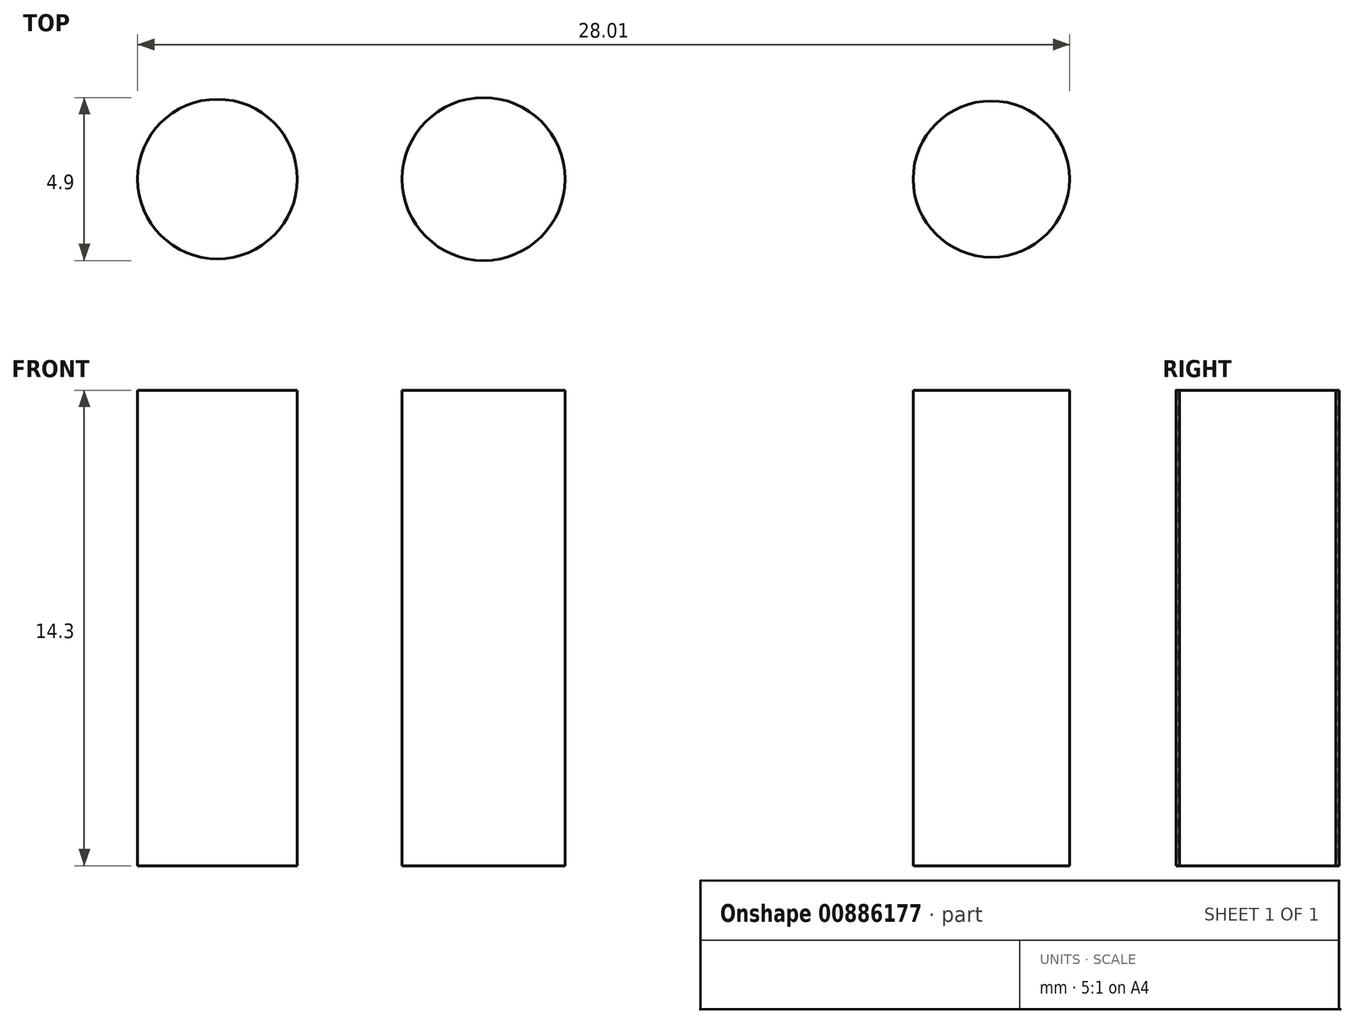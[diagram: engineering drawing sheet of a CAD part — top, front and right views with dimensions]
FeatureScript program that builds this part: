
annotation { "Feature Type Name" : "Feature", "Feature Type Description" : "" }
export const myFeature = defineFeature(function(context is Context, id is Id, definition is map)
    precondition{}
    {
        {
            var Q0;
            Q0=qCreatedBy(makeId("Top.planeOp"), FACE);
            var sketch = newSketch(context, id + "F0", { "sketchPlane" : qUnion([Q0])});
            skCircle(sketch, "E0", {"center": v(0, 0) * mm, "radius": 2.45 * mm});
            skCircle(sketch, "E1", {"center": v(-8, 0) * mm, "radius": 2.4 * mm});
            skCircle(sketch, "E2", {"center": v(15.26, 0) * mm, "radius": 2.35 * mm});
            skSolve(sketch);
        }
        {
            var Q0;
            Q0 = qSketchRegion(id + "F0", true);
            extrude(context, id + "F1", {"entities" : qUnion([Q0]), "depth" : 14.3 * mm, "offsetDistance" : 25 * mm});
        }
    });
